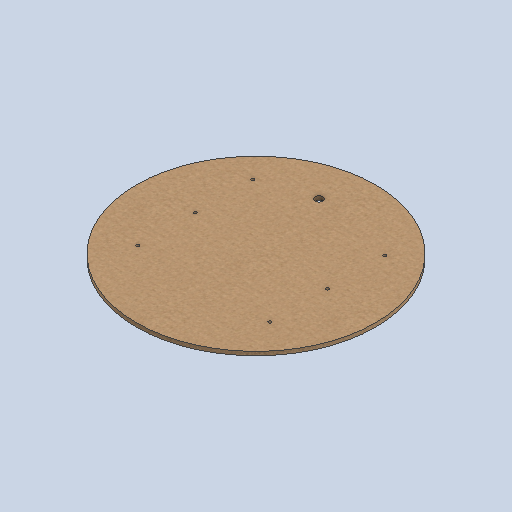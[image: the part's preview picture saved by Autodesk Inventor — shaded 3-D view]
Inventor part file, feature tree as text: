
AUTODESK INVENTOR PART (.ipt)
format: ipt  version: 2023 (Build 270158000, 158)  size: 256,512 bytes
history: native  units: mm
features: sketch x3, extrude x2, other x1, hole x1
ambient origin geometry x8: Origin, YZ Plane, XZ Plane, XY Plane, X Axis, Y Axis, Z Axis, Center Point
bodies: Body1 (feature_tree)
feature tree (7):
  other  "ソリッド1"
  extrude  "押し出し1"  Depth=250.0mm
  extrude  "押し出し2"  Depth=4.0mm TaperAngle=0.0deg
  hole  "穴1"  [1 undecoded]
  sketch  "スケッチ1"
  sketch  "スケッチ2"
  sketch  "スケッチ4"
note: 1 required parameter value undecoded (feature->parameter linkage not recoverable at this tier; creation-order binding heuristic only, values carry confidence <= 0.55)
